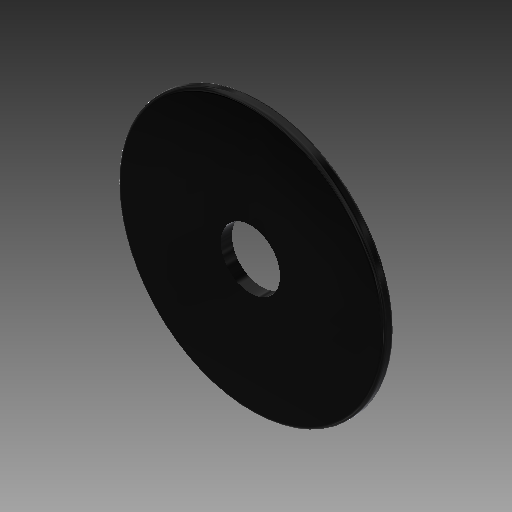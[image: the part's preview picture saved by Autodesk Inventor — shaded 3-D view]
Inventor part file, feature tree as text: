
AUTODESK INVENTOR PART (.ipt)
format: ipt  version: 2019 (Build 230136000, 136)  size: 124,416 bytes
history: native  units: in
note: dims shown in document units (in); Inventor stores cm internally (conversion verified against a paired STEP export)
features: extrude x1, fillet x1, sketch x1
ambient origin geometry x8: Origin, YZ Plane, XZ Plane, XY Plane, X Axis, Y Axis, Z Axis, Center Point
bodies: Solid1 (feature_tree)
feature tree (3):
  extrude  "Ring"  Depth=0.0197in
  fillet  "Fillet1"  Radius=0.0591in
  sketch  "Sketch"  dims[d0=0.315in d1=1.4173in d2=0.0591in d3=0.0in d4=0.0197in]
